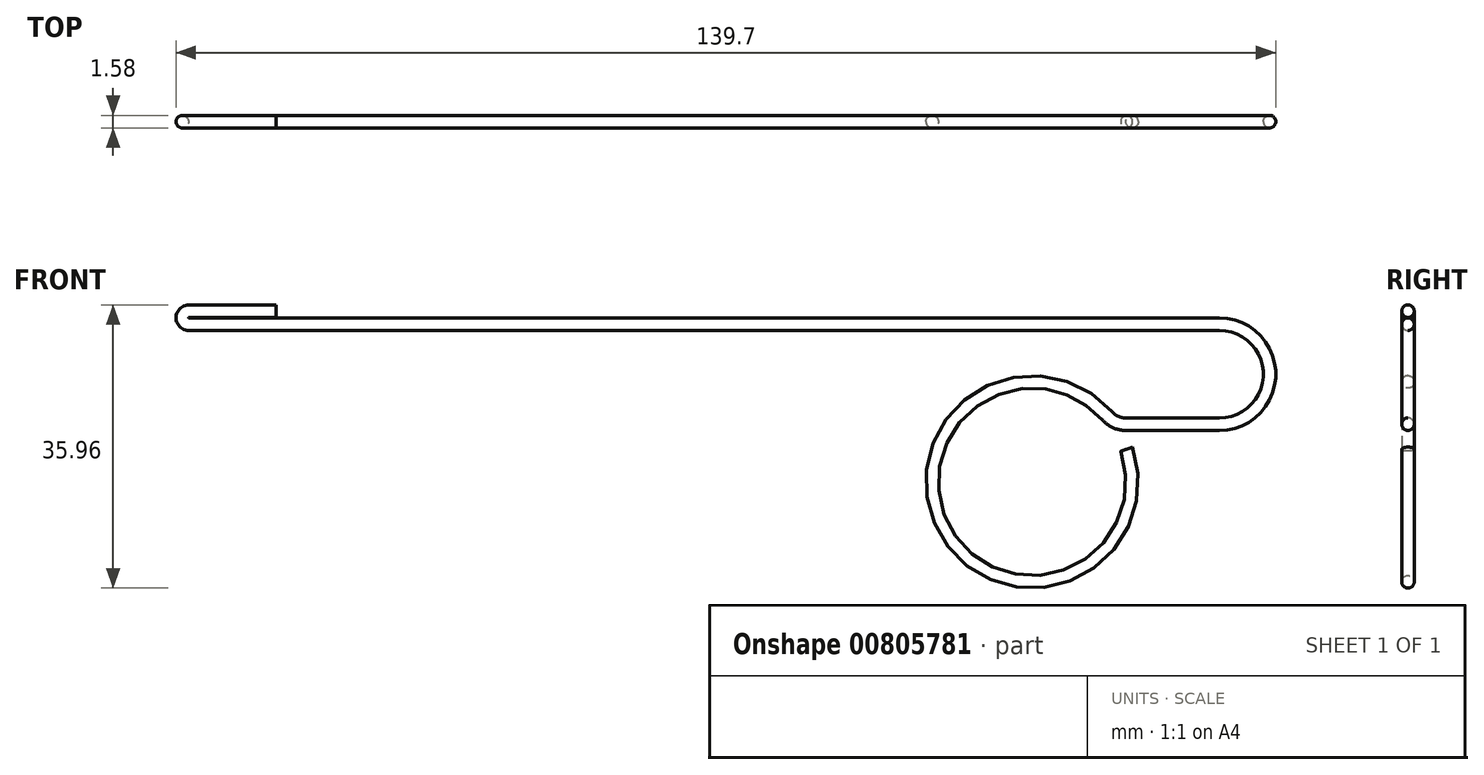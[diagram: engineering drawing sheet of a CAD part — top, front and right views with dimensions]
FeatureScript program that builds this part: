
annotation { "Feature Type Name" : "Feature", "Feature Type Description" : "" }
export const myFeature = defineFeature(function(context is Context, id is Id, definition is map)
    precondition{}
    {
        {
            var Q0;
            Q0=qCreatedBy(makeId("Front.planeOp"),FACE);
            var sketch = newSketch(context, id + "F0", { "sketchPlane" : qUnion([Q0])});
            skLineSegment(sketch, "E0", {"start": v(-130.94, 6.35) * mm, "end": v(0, 6.35) * mm});
            skArc(sketch, "E1", {"start": v(0, -6.35) * mm, "mid": v(6.35, 0) * mm, "end": v(0, 6.35) * mm});
            skLineSegment(sketch, "E2", {"start": v(0, -6.35) * mm, "end": v(-11.9, -6.35) * mm});
            skArc(sketch, "E3", {"start": v(-14.29, -5.28) * mm, "mid": v(-34.78, -20.07) * mm, "end": v(-11.8, -9.53) * mm});
            skArc(sketch, "E4.filletArc", {"start": v(-14.29, -5.28) * mm, "mid": v(-13.21, -6.07) * mm, "end": v(-11.9, -6.35) * mm});
            skArc(sketch, "E5", {"start": v(-130.94, 6.35) * mm, "mid": v(-131.76, 7.18) * mm, "end": v(-130.94, 8) * mm});
            skLineSegment(sketch, "E6", {"start": v(-130.94, 8) * mm, "end": v(-119.82, 8) * mm});
            skLineSegment(sketch, "E7", {"start": v(6.35, 0) * mm, "end": v(6.35, -37.86) * mm, "construction": true});
            skSolve(sketch);
        }
        {
            var Q0;
            Q0=qCreatedBy(makeId("Right.planeOp"),FACE);
            var Q1;
            Q1=sQuery(id+"F0.wireOp",VERTEX,"E0.start");
            cPlane(context, id + "F1", {"entities" : qUnion([Q0, Q1]), "cplaneType" : CPlaneType.PLANE_POINT, "offset" : 25.4 * mm, "width" : 152.4 * mm, "height" : 152.4 * mm});
        }
        {
            var Q0;
            Q0=qCreatedBy(id+"F1.planeOp",FACE);
            var sketch = newSketch(context, id + "F2", { "sketchPlane" : qUnion([Q0])});
            skCircle(sketch, "E8", {"center": v(0, 6.35) * mm, "radius": 0.8 * mm});
            skSolve(sketch);
        }
        {
            var Q0;
            Q0=makeQuery(id+"F2.imprint","IMPRINT",FACE,{"disambiguationData":[TD([[makeQuery(id+"F2.imprint","IMPRINT",EDGE,{"derivedFrom":sQuery(id+"F2.wireOp",EDGE,"E8")}),1.0]])]});
            var Q1;
            Q1=sQuery(id+"F0.wireOp",EDGE,"E0");
            var Q2;
            Q2=sQuery(id+"F0.wireOp",EDGE,"E1");
            var Q3;
            Q3=sQuery(id+"F0.wireOp",EDGE,"3PA9Kher-cZht-PNjC-O8Yc-99URsSATVKox");
            var Q4;
            Q4=sQuery(id+"F0.wireOp",EDGE,"pwyfp6wE-sNyc-sEfW-1gPu-OnvCayY2sXo7");
            var Q5;
            Q5=sQuery(id+"F0.wireOp",EDGE,"E2");
            var Q6;
            Q6=sQuery(id+"F0.wireOp",EDGE,"E4.filletArc");
            var Q7;
            Q7=sQuery(id+"F0.wireOp",EDGE,"IhQoeiGo-s2SB-GYpc-DPfG-hOOTRYYXMwEX");
            var Q8;
            Q8=sQuery(id+"F0.wireOp",EDGE,"e8c4de61-7e0b-466f-88d6-5a93511e19b9.filletArc");
            var Q9;
            Q9=sQuery(id+"F0.wireOp",EDGE,"aGGvM1t8-AfPq-d0EH-jgef-NmA0p4jWmkoe");
            var Q10;
            Q10=sQuery(id+"F0.wireOp",EDGE,"E3");
            var Q11;
            Q11=sQuery(id+"F0.wireOp",EDGE,"E5");
            var Q12;
            Q12=sQuery(id+"F0.wireOp",EDGE,"E6");
            sweep(context, id + "F3", {"profiles" : qUnion([Q0]), "path" : qUnion([Q1, Q2, Q3, Q4, Q5, Q6, Q7, Q8, Q9, Q10, Q11, Q12])});
        }
    });
